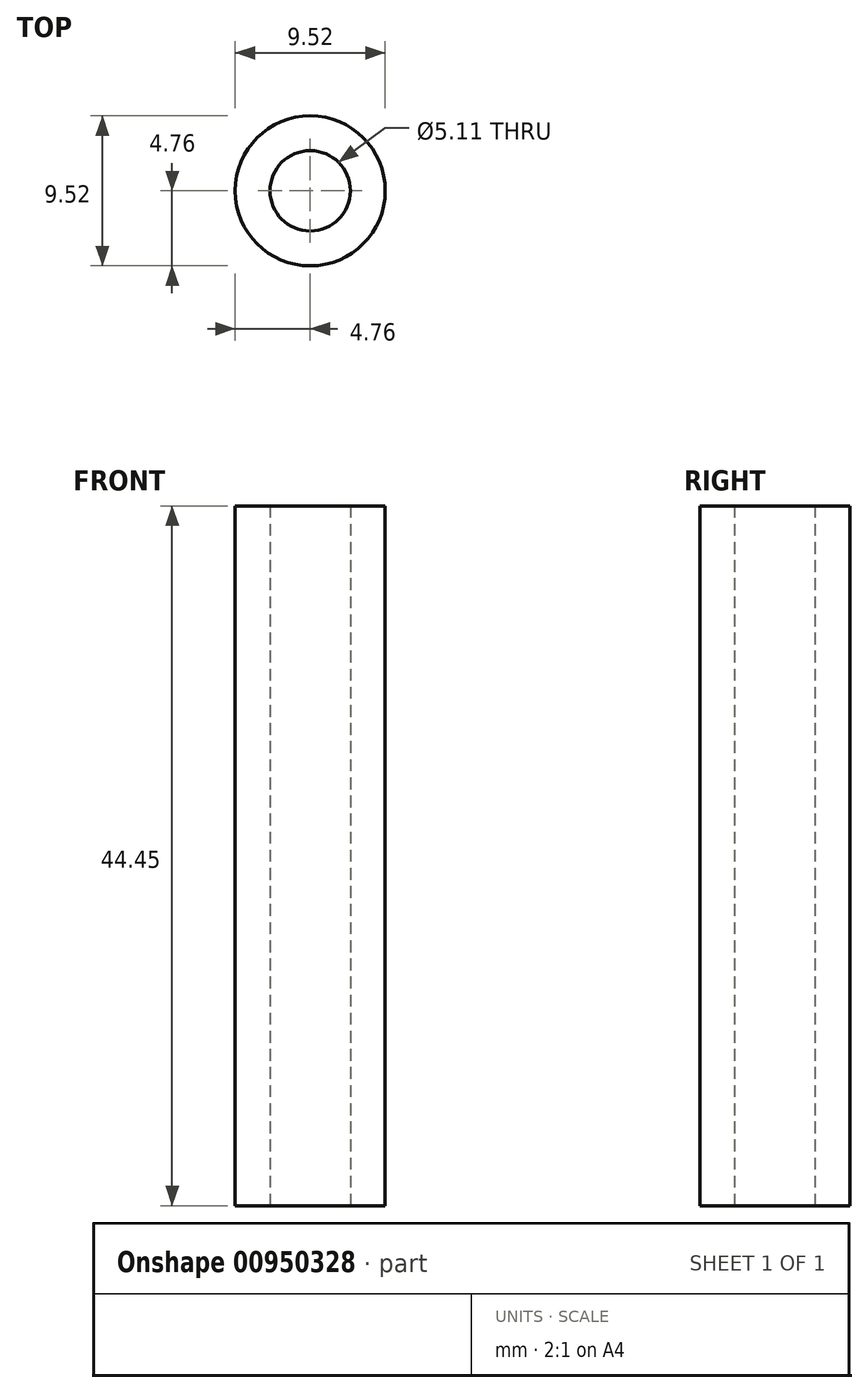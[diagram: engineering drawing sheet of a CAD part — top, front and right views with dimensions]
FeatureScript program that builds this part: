
annotation { "Feature Type Name" : "Feature", "Feature Type Description" : "" }
export const myFeature = defineFeature(function(context is Context, id is Id, definition is map)
    precondition{}
    {
        {
            var Q0;
            Q0=qCreatedBy(makeId("Top.planeOp"),FACE);
            var sketch = newSketch(context, id + "F0", { "sketchPlane" : qUnion([Q0])});
            skCircle(sketch, "E0", {"center": v(0, 0) * mm, "radius": 2.55 * mm});
            skCircle(sketch, "E1", {"center": v(0, 0) * mm, "radius": 4.76 * mm});
            skSolve(sketch);
        }
        {
            var Q0;
            Q0=makeQuery(id+"F0.imprint","IMPRINT",FACE,{"disambiguationData":[TD([[makeQuery(id+"F0.imprint","IMPRINT",EDGE,{"derivedFrom":sQuery(id+"F0.wireOp",EDGE,"E0")}),-1.0]])]});
            extrude(context, id + "F1", {"entities" : qUnion([Q0]), "depth" : 44.45 * mm, "offsetDistance" : 25.4 * mm});
        }
    });
